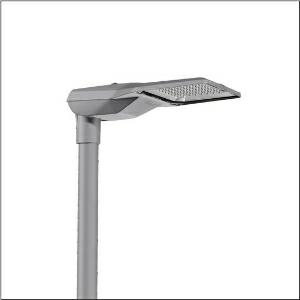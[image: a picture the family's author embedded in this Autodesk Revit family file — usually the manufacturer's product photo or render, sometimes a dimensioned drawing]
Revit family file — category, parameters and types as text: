
# Revit family: streetlight_sl_21_midi___st0_8a_5xe3c33s08nb_db16
name_source: partatom
category: Lighting Fixtures
units: mm (PartAtom-declared; Revit-internal decimal feet)

## family parameters
Cut with Voids When Loaded = No
Host = Face
Light Source = No
Part Type = Normal
Room Calculation Point = No
Round Connector Dimension = Use Diameter
Shared = No

## types (1)
- --- (1 x LED, 22700 lm, 151.2 W, 3000K)
    Apparent Load = 151 VA
    CIE Flux Codes = 41 75 97 100 100
    Color Rendering = 70
    Color Temperature = 3000K
    Default Elevation = 1800 mm
    Description = Streetlight SL 21 midi, mast luminaire, primary light control with lens, of PMMA, primary optical cover: cover, of toughened safety glass, transparent, light distribution: ST0.8a, light emission: direct distribution, primary light characteristic: asymmetric, installation type: side-entry, post-top, LED, High Power LED, rated luminous flux: 22.700lm, luminous efficacy: 150lm/W, light colour: 730, colour temperature: 3000K, control gear: D4i, control: overheat protection, constant luminous flux control, time-dependent luminous flux control, flexible luminous flux parameterisation, pre-setting: logarithmic dimming characteristic, mains connection: 230..240V, AC, 50/60Hz, start of lifetime: 151W, end of service life: 157W, reduction: 70W, luminaire housing, of diecast aluminium, powder-coated, SITECO metallic grey (DB 702S), corrosivity category C5 high according to DIN EN ISO 12944, please order mast flange separately, inclination adjustable: 0°, 5°, 10°, 15°, sealing non-destructively replaceable, multi-level sealing system, length: 644mm, width: 335mm, height: 110mm, mast flange for spigot size: 42mm (side-entry): 5XC10008XM4, 60/48mm (side-entry/post-top): 5XC10108XM2, 76/60mm (side-entry/post-top): 5XC10108XM1, mounting height: 4..8m, Smart Interface above, protection rating (complete): IP66, insulation class (complete): insulation class II (safety insulation), certification: CE, ENEC, ENEC+, VDE, impact resistance: IK10, permissible operating ambient temperature for outdoor applications: -40..+50°C, standard-compliant lighting for roads and squares, packaging unit: 1 piece

Light Distribution: ST0.8a
    Height = 111 mm
    Lamp = 1 x LED
    Lamp Light Flux = 22700 lm
    Lamp Power = 151.2 W
    Lamp count = 1
    Length = 644 mm
    Luminous efficacy = 150 lm/W
    Manufacturer = Siteco
    ModVariant = No
    Model = 5XE3C33S08NB
    Number of Poles = 1
    OnlyDefault = Yes
    Power Factor = 1
    Product Name = Streetlight SL 21 midi | ST0.8a
    Product group = mast luminaire | pylon top
    ProductGroupID = 6100
    Protection Class = Protection class II
    Protection Degree = IP 66
    RLX_Detail_Level = 1
    RLX_Emergency_Light_Flux = 0 lm
    RLX_Emergency_Type = 0
    RLX_Emergency_Type_DB = No
    RlxData = <blob elided: 26945 chars, md5=98edd48d>
    Socket = socket
    Standby Power = 0 W
    System Light Flux = 22700 lm
    System Power = 151 W
    Type Comments = factory setting: luminous flux: 100 % | dim-lin: 254 | 802 mA
    Type Image = l_1004302.jpg
    URL = http://relux.com
    VarID = @adj_168235
    Voltage = 0 V
    Weight = 0.00 kg
    Width = 336 mm

## geometry (parser evidence)
native form markers: Blend x4, Sweep x10
no freeform markers — native parametric forms only
